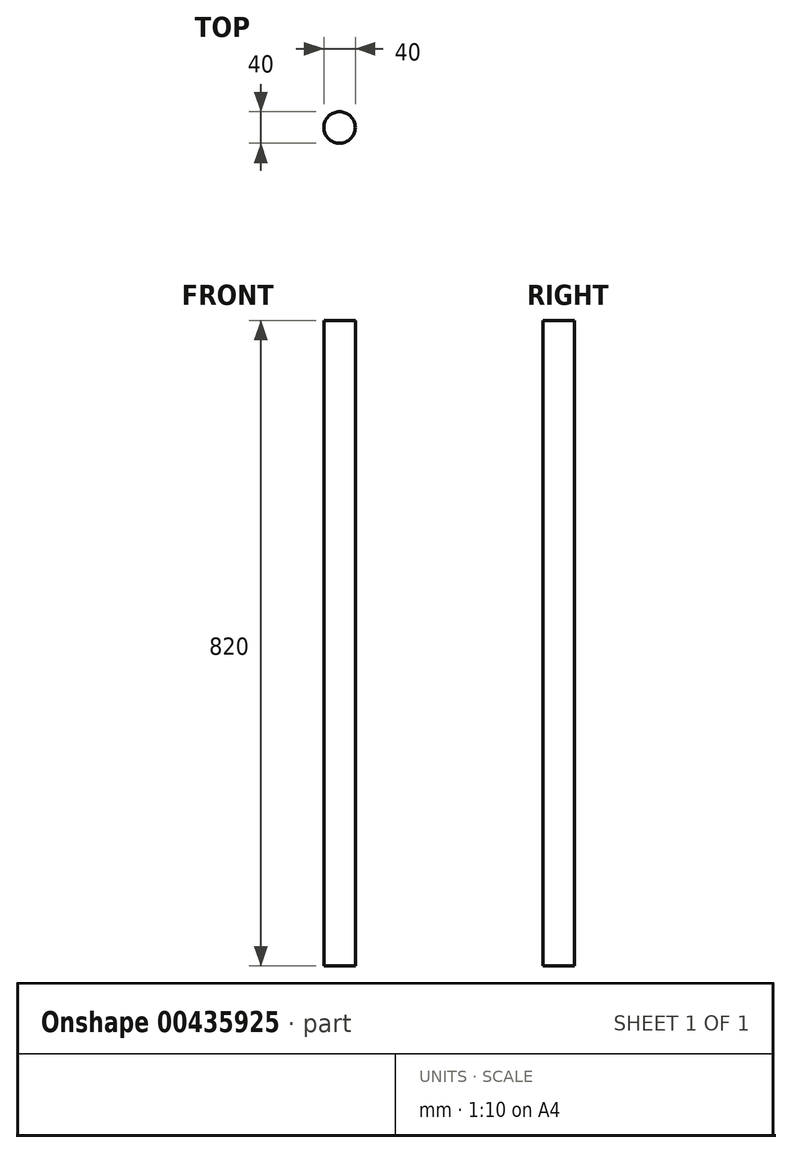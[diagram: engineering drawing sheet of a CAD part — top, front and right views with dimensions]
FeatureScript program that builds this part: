
annotation { "Feature Type Name" : "Feature", "Feature Type Description" : "" }
export const myFeature = defineFeature(function(context is Context, id is Id, definition is map)
    precondition{}
    {
        {
            var Q0;
            Q0=qCreatedBy(makeId("Top.planeOp"),FACE);
            var sketch = newSketch(context, id + "F0", { "sketchPlane" : qUnion([Q0])});
            skCircle(sketch, "E0", {"center": v(0, 0) * mm, "radius": 20 * mm});
            skSolve(sketch);
        }
        {
            var Q0;
            Q0=makeQuery(id+"F0.imprint","IMPRINT",FACE,{"disambiguationData":[TD([[makeQuery(id+"F0.imprint","IMPRINT",EDGE,{"derivedFrom":sQuery(id+"F0.wireOp",EDGE,"E0")}),1.0]])]});
            var Q1;
            Q1=sQuery(id+"F0.wireOp",EDGE,"E0");
            extrude(context, id + "F1", {"entities" : qUnion([Q0]), "surfaceEntities" : qUnion([Q1]), "depth" : 820 * mm});
        }
    });
